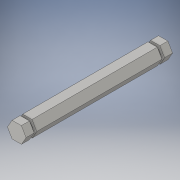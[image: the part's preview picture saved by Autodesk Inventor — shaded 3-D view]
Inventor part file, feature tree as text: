
AUTODESK INVENTOR PART (.ipt)
format: ipt  version: 2016 (Build 200138000, 138)  size: 127,488 bytes
history: native  units: in
note: dims shown in document units (in); Inventor stores cm internally (conversion verified against a paired STEP export)
features: extrude x5, sketch x5, projected_geometry x2
ambient origin geometry x8: Origin, YZ Plane, XZ Plane, XY Plane, X Axis, Y Axis, Z Axis, Center Point
bodies: Solid1 (feature_tree)
feature tree (12):
  extrude  "Extrusion1"  Depth=3.879in TaperAngle=0.0deg
  extrude  "Extrusion2"  Depth=0.0787in TaperAngle=0.0deg
  extrude  "Extrusion3"  Depth=0.0787in TaperAngle=0.0deg
  extrude  "Extrusion4"  Depth=0.25in TaperAngle=0.0deg
  extrude  "Extrusion5"  [1 undecoded]
  sketch  "Sketch1"  dims[d0=0.5in d1=3.879in d2=0.0in]
  sketch  "Sketch2"  dims[d3=0.33in d4=0.0787in d5=0.0in]
  sketch  "Sketch3"  dims[d6=0.33in d7=0.0787in d8=0.0in]
  sketch  "Sketch4"  dims[d9=0.25in d10=0.0in d11=0.25in d12=0.0in]
  projected_geometry  "Projected Loop1"
  sketch  "Sketch5"
  projected_geometry  "Projected Loop2"
note: 1 required parameter value undecoded (feature->parameter linkage not recoverable at this tier; creation-order binding heuristic only, values carry confidence <= 0.55)
